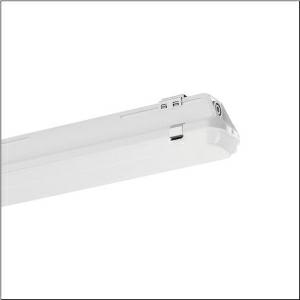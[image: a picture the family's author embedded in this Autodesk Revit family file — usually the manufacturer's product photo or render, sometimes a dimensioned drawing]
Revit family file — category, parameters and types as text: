
# Revit family: monsun_r__21_51fb107l440k_cbf5
name_source: partatom
category: Lighting Fixtures
units: mm (PartAtom-declared; Revit-internal decimal feet)

## family parameters
Cut with Voids When Loaded = No
Host = Face
Light Source = No
Part Type = Normal
Room Calculation Point = No
Round Connector Dimension = Use Diameter
Shared = No

## types (1)
- Monsun® 21 (1 x LED, 4350 lm, 24.7 W, 4000K)
    Apparent Load = 25 VA
    CIE Flux Codes = 46 76 93 94 100
    Color Rendering = 80
    Color Temperature = 4000K
    Default Elevation = 1800 mm
    Description = Monsun® 21, damp-proof luminaire, chain hanger, primary optical cover: enclosure, of PMMA, light emission: direct distribution, primary light characteristic: symmetric, installation type: suspended mounting, surface-mounted, horizontal mounting, vertical mounting, LED, rated luminous flux: 4.350lm, luminous efficacy: 176lm/W, light colour: 840, colour temperature: 4000K, control gear: ON/OFF, with terminal, 3-pole, max. 2.5mm², mains connection: 220..240V, AC, 50/60Hz, rated input power: 25W, housing, of glass-fibre reinforced plastic, uncoated, bright grey, incl. chain hanger, length: 1.299mm, width: 90mm, height: 88mm, clip for enclosure, of stainless steel (V2A), ceiling mounting element, of stainless steel (V2A), chain hanger, of stainless steel (V2A), protection rating (complete): IP66, insulation class (complete): insulation class I (protective earthing), certification: CE, ENEC, VDE, UKCA, protection symbol: D, impact resistance: IK04, permissible operating ambient temperature: -25..+35°C, standard: EN 50419, EN 60598-2-1, corresponds to IFS (International Featured Standards) requirements for safety and quality in the food industry, for indoor or canopied outdoor use, no direct snow, no direct sun, no direct rain, LABS conformity tested according to VDMA 24364:2018-05, contact your sales advisor before using the luminaires in applications with unclear chemical exposure, large temperature fluctuations or condensation-forming humidity, packaging unit: 1 piece
    Height = 88 mm
    Lamp = 1 x LED
    Lamp Light Flux = 4350 lm
    Lamp Power = 24.7 W
    Lamp count = 1
    Length = 1299 mm
    Luminous efficacy = 176 lm/W
    Manufacturer = Siteco
    ModVariant = No
    Model = 51FB107L440K
    Mounting Place = Ceiling
    Mounting Type = Surface mounted
    Number of Poles = 1
    OnlyDefault = Yes
    Power Factor = 1
    Product Name = Monsun® 21
    Product group = damp-proof luminaire
    ProductGroupID = 301
    Protection Class = Protection class I
    Protection Degree = IP 66
    RLX_Detail_Level = 1
    RLX_Emergency_Light_Flux = 0 lm
    RLX_Emergency_Type = 0
    RLX_Emergency_Type_DB = No
    RlxData = <blob elided: 89877 chars, md5=7ac70cb6>
    Socket = socket
    Standby Power = 0 W
    System Light Flux = 4350 lm
    System Power = 25 W
    Type Comments = Product without accessories
    Type Image = l_1319656.jpg
    URL = http://relux.com
    VarID = ---
    Voltage = 0 V
    Weight = 0.00 kg
    Width = 90 mm

## geometry (parser evidence)
native form markers: Blend x4, Sweep x13
no freeform markers — native parametric forms only
